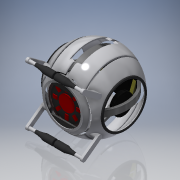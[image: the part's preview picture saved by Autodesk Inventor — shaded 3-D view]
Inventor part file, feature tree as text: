
AUTODESK INVENTOR PART (.ipt)
format: ipt  version: 2019 (Build 230136000, 136)  size: 1,242,112 bytes
history: native  units: in
note: dims shown in document units (in); Inventor stores cm internally (conversion verified against a paired STEP export)
features: sketch x28, extrude x26, mirror x12, plane x9, projected_geometry x8, delete_face x5, fillet x4, revolve x3, shell x1, pattern_circular x1
ambient origin geometry x8: Origin, YZ Plane, XZ Plane, XY Plane, X Axis, Y Axis, Z Axis, Center Point
bodies: Solid1 (feature_tree)
feature tree (97):
  revolve  "Revolution1"  Angle=180.0deg
  plane  "Work Plane1"
  extrude  "Extrusion1"  Depth=2.5in
  shell  "Shell1"  Thickness=7.4375in
  extrude  "Extrusion4"  Depth=0.75in TaperAngle=0.0deg
  plane  "Work Plane2"
  extrude  "Extrusion5"  Depth=2.4375in TaperAngle=0.0deg
  plane  "Work Plane3"
  extrude  "Extrusion6"  Depth=0.25in TaperAngle=0.0deg
  extrude  "Extrusion7"  Depth=2.375in
  plane  "Work Plane4"
  extrude  "Extrusion8"  Depth=8.0375in TaperAngle=0.0deg
  mirror  "Mirror3"
  plane  "Work Plane5"
  extrude  "Extrusion9"  Depth=3.99in
  extrude  "Extrusion10"  Depth=0.5in TaperAngle=0.0deg
  pattern_circular  "Circular Pattern1"  Count=2 Angle=90.0deg
  extrude  "Extrusion11"  Depth=0.0625in TaperAngle=0.0deg
  extrude  "Extrusion12"  Depth=0.625in TaperAngle=0.0deg
  extrude  "Extrusion13"  Depth=0.0625in
  mirror  "Mirror4"
  extrude  "Extrusion14"  Depth=0.0625in TaperAngle=0.0deg
  mirror  "Mirror5"
  extrude  "Extrusion15"  Depth=0.9in
  fillet  "Fillet2"  Radius=0.5in
  mirror  "Mirror6"
  extrude  "Extrusion16"  Depth=1.1875in TaperAngle=0.0deg
  plane  "Work Plane10"
  sketch  "Sketch24"  dims[d84=0.4375in d99=180.0deg]
  extrude  "Extrusion17"  TaperAngle=180.0deg  [1 undecoded]
  extrude  "Extrusion18"  Depth=3.5in
  mirror  "Mirror9"
  mirror  "Mirror10"
  fillet  "Fillet3"  Radius=0.1in
  delete_face  "Delete Face2"
  delete_face  "Delete Face3"
  sketch  "Sketch28"  dims[d100=0.3607in d101=3.5in d102=0.1in]
  revolve  "Revolution6"  [1 undecoded]
  revolve  "Revolution7"  Angle=180.0deg
  mirror  "Mirror11"
  plane  "Work Plane11"
  extrude  "Extrusion22"  Depth=0.5in TaperAngle=0.0deg
  delete_face  "Delete Face4"
  delete_face  "Delete Face5"
  delete_face  "Delete Face6"
  extrude  "Extrusion23"  [1 undecoded]
  extrude  "Extrusion24"  Depth=0.5in TaperAngle=0.0deg
  extrude  "Extrusion25"  Depth=1.5in
  plane  "Work Plane12"
  extrude  "Extrusion26"  Depth=0.25in
  mirror  "Mirror12"
  extrude  "Extrusion27"  Depth=0.25in
  mirror  "Mirror13"
  extrude  "Extrusion28"  [1 undecoded]
  mirror  "Mirror14"
  extrude  "Extrusion29"  Depth=0.8125in TaperAngle=0.0deg
  plane  "Work Plane13"
  extrude  "Extrusion30"  Depth=0.0625in TaperAngle=0.0deg
  mirror  "Mirror15"
  mirror  "Mirror16"
  fillet  "Fillet4"  Radius=0.025in
  sketch  "Sketch39"  dims[d130=0.5in d131=0.8125in d132=0.0in]
  extrude  "Extrusion31"  [1 undecoded]
  fillet  "Fillet5"  [1 undecoded]
  sketch  "Sketch1"  dims[d0=6.0in d1=180.0deg]
  sketch  "Sketch2"  dims[d2=2.5in d3=3.25in d4=7.4375in d5=0.0in]
  sketch  "Sketch5"  dims[d6=0.1in d17=0.75in d18=0.0in]
  sketch  "Sketch6"  dims[d20=-0.125in d21=2.4375in d22=0.0in]
  sketch  "Sketch7"  dims[d23=-0.125in d24=0.25in d25=0.0in]
  sketch  "Sketch8"  dims[d26=0.025in d27=0.0in d28=2.375in]
  sketch  "Sketch9"  dims[d29=3.75in d30=8.0375in d31=0.0in]
  sketch  "Sketch10"  dims[d32=-2.25in d33=3.99in]
  sketch  "Sketch11"  dims[d34=8.0375in d35=0.0in d36=0.5in d37=0.0in d38=0.7874in d39=90.0deg]
  sketch  "Sketch12"  dims[d41=0.0625in d42=0.0in d43=0.3125in d44=0.0in]
  sketch  "Sketch13"  dims[d45=0.3125in d46=0.0in d47=0.625in d48=0.0in]
  sketch  "Sketch14"  dims[d49=0.125in d50=0.0in d51=0.0625in]
  sketch  "Sketch15"  dims[d52=3.1496in d54=360.0deg d56=0.0625in d57=0.0in]
  sketch  "Sketch16"  dims[d75=2.1875in d78=0.9in d79=0.5in]
  sketch  "Sketch17"  dims[d80=1.125in d81=0.0in d82=1.1875in d83=0.0in]
  sketch  "Sketch29"  dims[d103=0.1in d104=1.0in d105=0.0in]
  sketch  "Sketch30"  dims[d106=0.5in d107=0.0in d108=180.0deg]
  sketch  "Sketch31"  dims[d109=0.0in d110=0.5in d111=0.0in]
  sketch  "Sketch32"  dims[d112=0.625in d113=0.0in d114=-0.5in]
  sketch  "Sketch34"  dims[d115=0.375in d116=0.5in d117=0.0in]
  sketch  "Sketch35"  dims[d118=1.5in d119=0.2508in]
  sketch  "Sketch36"  dims[d121=0.1875in d122=0.0in d123=0.25in]
  sketch  "Sketch37"  dims[d124=3.75in d125=0.0in d126=0.25in]
  sketch  "Sketch38"  dims[d127=28.4375in d128=0.0in d129=-0.75in]
  sketch  "Sketch40"  dims[d133=2.25in d134=0.0625in d135=0.0in d136=0.025in]
  projected_geometry  "Project Cut Edges1"
  projected_geometry  "Project Cut Edges2"
  projected_geometry  "Project Cut Edges7"
  projected_geometry  "Project Cut Edges8"
  projected_geometry  "Project Cut Edges9"
  projected_geometry  "Project Cut Edges10"
  projected_geometry  "Project Cut Edges12"
  projected_geometry  "Project Cut Edges13"
note: 6 required parameter values undecoded (feature->parameter linkage not recoverable at this tier; creation-order binding heuristic only, values carry confidence <= 0.55)